# Revit family: ERA_LF_SPP-411
name_source: partatom
category: Осветительные приборы
units: mm (PartAtom-declared; Revit-internal decimal feet)

## family parameters
Всегда вертикально = Да
Источник света = Да
На основе рабочей плоскости = Нет
Общий = Нет
При загрузке вырезать с полостями = Нет
Размер круглого соединителя = Использовать диаметр
Тип детали = Нормальный
Точка расчета площади = Да

## types (1)
- ERA_LF_SPP-411
    ADSK_Единица измерения = шт.
    ADSK_Завод-изготовитель = ЭРА
    ADSK_Классификация нагрузок = Освещение
    ADSK_Код изделия = SPP-411-0-50K-100
    ADSK_Количество фаз = 1
    ADSK_Коэффициент мощности = 0.95
    ADSK_Марка = SPP-411-0-50K-100
    ADSK_Наименование = Светильник, LED, круглый, подвесной, IP65, d 230,7х88 мм, 100 Вт, 5000 К, класс защиты I, в комплекте (ic-драйвер)
    ADSK_Наименование краткое = Светильник
    ADSK_Напряжение = 230 В
    ADSK_Номинальная мощность = 100 Вт
    ADSK_Обозначение = SPP-411
    ADSK_Полная мощность = 105 В·А
    ADSK_Примечание = IC-драйвер, закаленное стекло с тиснением "призма"
    ADSK_Размер_Высота = 88 мм
    ADSK_Размер_Диаметр = 230.7 мм
    URL = https://www.eraworld.ru
    Видимая форма излучения при визуализации = Нет
    Геометрия изделия = Круглый
    Диаметр подвеса = 1 мм
    Излучение по диаметру окружности = 230.7 мм
    Источник света = LED
    Класс защиты = I
    Класс пожароопасности = Нет
    Комплект = IC-драйвер
    Светофильтр = 16777215
    Смещение цветовой температуры при затухании лампы = <Нет>
    Степень защиты IP = IP65
    Тип установки = Подвесной
    Угол наклона = 90,00°
    Файл фотометрической сетки = IES для SPP-411-0-50K-100.ies
    Цвет = Чёрный
